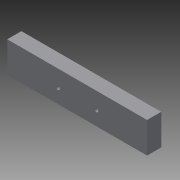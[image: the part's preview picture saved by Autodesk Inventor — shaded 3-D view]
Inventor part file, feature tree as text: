
AUTODESK INVENTOR PART (.ipt)
format: ipt  version: 2013 (Build 170138000, 138)  size: 169,984 bytes
history: native  units: mm
features: sketch x5, extrude x4, other x2, hole x1, fillet x1
ambient origin geometry x8: Origin, YZ Plane, XZ Plane, XY Plane, X Axis, Y Axis, Z Axis, Center Point
feature tree (13):
  other  "ソリッド1"
  extrude  "押し出し1"  Depth=109.0mm
  extrude  "押し出し3"  Depth=54.5mm
  extrude  "押し出し4"  Depth=20.0mm
  extrude  "押し出し5"  Depth=10.0mm
  hole  "穴1"  [1 undecoded]
  other  "リップ3"
  fillet  "フィレット1"  Radius=11.0mm
  sketch  "スケッチ1"
  sketch  "スケッチ4"
  sketch  "スケッチ5"
  sketch  "スケッチ6"
  sketch  "スケッチ7"
note: 1 required parameter value undecoded (feature->parameter linkage not recoverable at this tier; creation-order binding heuristic only, values carry confidence <= 0.55)
